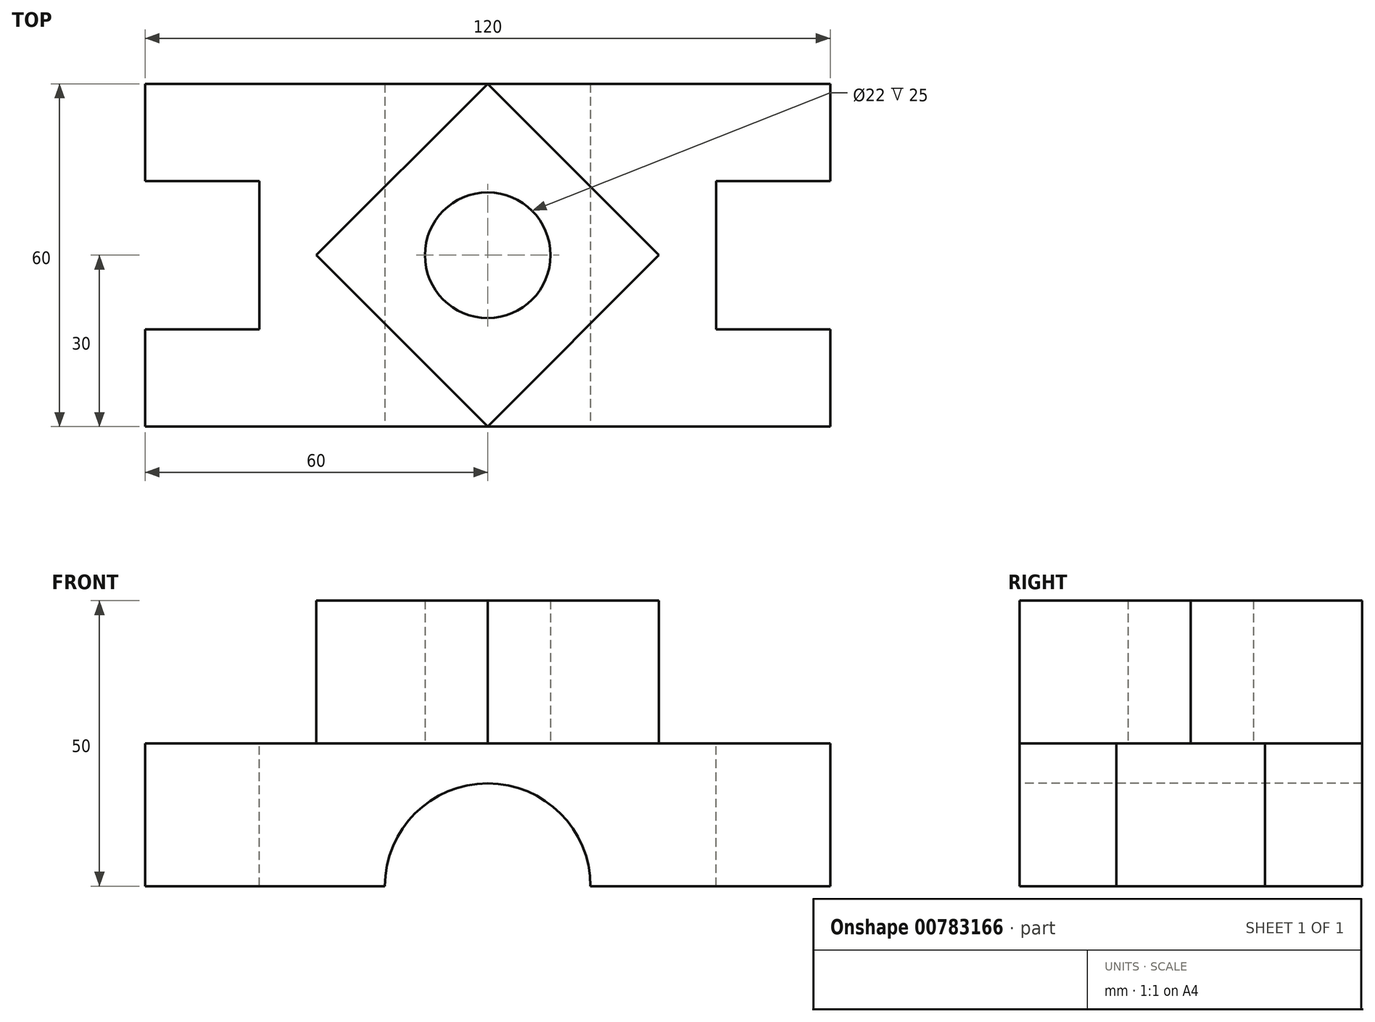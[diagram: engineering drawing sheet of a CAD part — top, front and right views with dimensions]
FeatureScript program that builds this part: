
annotation { "Feature Type Name" : "Feature", "Feature Type Description" : "" }
export const myFeature = defineFeature(function(context is Context, id is Id, definition is map)
    precondition{}
    {
        {
            var Q0;
            Q0=qCreatedBy(makeId("Top.planeOp"),FACE);
            var sketch = newSketch(context, id + "F0", { "sketchPlane" : qUnion([Q0])});
            skLineSegment(sketch, "E0.bottom", {"start": v(60, -30) * mm, "end": v(-60, -30) * mm});
            skLineSegment(sketch, "E0.top", {"start": v(60, 30) * mm, "end": v(-60, 30) * mm});
            skLineSegment(sketch, "E0.left", {"start": v(60, -30) * mm, "end": v(60, 30) * mm});
            skLineSegment(sketch, "E0.right", {"start": v(-60, -30) * mm, "end": v(-60, 30) * mm});
            skPoint(sketch, "E0.middle", {"position": v(0, 0) * mm});
            skSolve(sketch);
        }
        {
            var Q0;
            Q0=makeQuery(id+"F0.imprint","IMPRINT",FACE,{"disambiguationData":[TD([[makeQuery(id+"F0.imprint","IMPRINT",EDGE,{"derivedFrom":sQuery(id+"F0.wireOp",EDGE,"E0.bottom")}),-1.0]])]});
            extrude(context, id + "F1", {"entities" : qUnion([Q0]), "depth" : 25 * mm, "offsetDistance" : 25 * mm});
        }
        {
            var Q0;
            Q0=makeQuery(id+"F1.opExtrude","CAP_FACE",FACE,{"disambiguationData":[OSD([sQuery(id+"F0.wireOp",EDGE,"E0.bottom"),sQuery(id+"F0.wireOp",EDGE,"E0.top"),sQuery(id+"F0.wireOp",EDGE,"E0.left"),sQuery(id+"F0.wireOp",EDGE,"E0.right")])],"isStart":false});
            var sketch = newSketch(context, id + "F2", { "sketchPlane" : qUnion([Q0])});
            skLineSegment(sketch, "E1.bottom", {"start": v(80, -13) * mm, "end": v(40, -13) * mm});
            skLineSegment(sketch, "E1.top", {"start": v(80, 13) * mm, "end": v(40, 13) * mm});
            skLineSegment(sketch, "E1.left", {"start": v(80, -13) * mm, "end": v(80, 13) * mm});
            skLineSegment(sketch, "E1.right", {"start": v(40, -13) * mm, "end": v(40, 13) * mm});
            skPoint(sketch, "E1.middle", {"position": v(60, 0) * mm});
            skSolve(sketch);
        }
        {
            var Q0;
            {var subQ0=sQuery(id+"F2.wireOp",EDGE,"E1.right");Q0=makeQuery(id+"F2.imprint","IMPRINT",FACE,{"disambiguationData":[TD([[makeQuery(id+"F2.imprint","IMPRINT",EDGE,{"derivedFrom":subQ0}),-1.0]])]});}
            extrude(context, id + "F3", {"entities" : qUnion([Q0]), "operationType" : NewBodyOperationType.REMOVE, "endBound" : BoundingType.THROUGH_ALL, "oppositeDirection" : true, "depth" : 25 * mm, "offsetDistance" : 25 * mm});
        }
        {
            var Q0;
            Q0=makeQuery(id+"F1.opExtrude","CAP_FACE",FACE,{"disambiguationData":[OSD([sQuery(id+"F0.wireOp",EDGE,"E0.bottom"),sQuery(id+"F0.wireOp",EDGE,"E0.top"),sQuery(id+"F0.wireOp",EDGE,"E0.left"),sQuery(id+"F0.wireOp",EDGE,"E0.right")])],"isStart":false});
            var sketch = newSketch(context, id + "F4", { "sketchPlane" : qUnion([Q0])});
            skLineSegment(sketch, "E2.bottom", {"start": v(-40, -13) * mm, "end": v(-80, -13) * mm});
            skLineSegment(sketch, "E2.top", {"start": v(-40, 13) * mm, "end": v(-80, 13) * mm});
            skLineSegment(sketch, "E2.left", {"start": v(-40, -13) * mm, "end": v(-40, 13) * mm});
            skLineSegment(sketch, "E2.right", {"start": v(-80, -13) * mm, "end": v(-80, 13) * mm});
            skPoint(sketch, "E2.middle", {"position": v(-60, 0) * mm});
            skSolve(sketch);
        }
        {
            var Q0;
            {var subQ0=sQuery(id+"F4.wireOp",EDGE,"E2.left");Q0=makeQuery(id+"F4.imprint","IMPRINT",FACE,{"disambiguationData":[TD([[makeQuery(id+"F4.imprint","IMPRINT",EDGE,{"derivedFrom":subQ0}),1.0]])]});}
            extrude(context, id + "F5", {"entities" : qUnion([Q0]), "operationType" : NewBodyOperationType.REMOVE, "endBound" : BoundingType.THROUGH_ALL, "oppositeDirection" : true, "depth" : 25 * mm, "offsetDistance" : 25 * mm});
        }
        {
            var Q0;
            Q0=makeQuery(id+"F1.opExtrude","SWEPT_FACE",FACE,{"disambiguationData":[OSD([sQuery(id+"F0.wireOp",EDGE,"E0.bottom")])]});
            var sketch = newSketch(context, id + "F6", { "sketchPlane" : qUnion([Q0])});
            skCircle(sketch, "E3", {"center": v(0, 0) * mm, "radius": 18 * mm});
            skSolve(sketch);
        }
        {
            var Q0;
            {var subQ0=sQuery(id+"F6.wireOp",EDGE,"E3");var subQ1=makeQuery(id+"F1.opExtrude","CAP_EDGE",EDGE,{"disambiguationData":[OSD([sQuery(id+"F0.wireOp",EDGE,"E0.bottom")])],"isStart":true});var subQ2=makeQuery(id+"F6.imprint","INTERSECT",VERTEX,{"disambiguationData":[OD(0.0)],"derivedFrom":[subQ1,subQ0]});Q0=makeQuery(id+"F6.imprint","IMPRINT",FACE,{"disambiguationData":[TD([[makeQuery(id+"F6.imprint","IMPRINT",EDGE,{"disambiguationData":[TD([[subQ2,-1.0]])],"derivedFrom":subQ0}),1.0]])]});}
            extrude(context, id + "F7", {"entities" : qUnion([Q0]), "operationType" : NewBodyOperationType.REMOVE, "oppositeDirection" : true, "depth" : 25 * mm, "offsetDistance" : 25 * mm});
        }
        {
            var Q0;
            Q0=makeQuery(id+"F7.boolean.opBoolean","COPY",FACE,{"derivedFrom":makeQuery(id+"F7.opExtrude","CAP_FACE",FACE,{"disambiguationData":[OSD([sQuery(id+"F0.wireOp",EDGE,"E0.bottom"),sQuery(id+"F6.wireOp",EDGE,"E3")])],"isStart":false})});
            extrude(context, id + "F8", {"entities" : qUnion([Q0]), "operationType" : NewBodyOperationType.REMOVE, "endBound" : BoundingType.THROUGH_ALL, "oppositeDirection" : true, "depth" : 25 * mm, "offsetDistance" : 25 * mm});
        }
        {
            var Q0;
            Q0=makeQuery(id+"F1.opExtrude","CAP_FACE",FACE,{"disambiguationData":[OSD([sQuery(id+"F0.wireOp",EDGE,"E0.bottom"),sQuery(id+"F0.wireOp",EDGE,"E0.top"),sQuery(id+"F0.wireOp",EDGE,"E0.left"),sQuery(id+"F0.wireOp",EDGE,"E0.right")])],"isStart":false});
            var sketch = newSketch(context, id + "F9", { "sketchPlane" : qUnion([Q0])});
            skCircle(sketch, "E4", {"center": v(0, 0) * mm, "radius": 11 * mm});
            skLineSegment(sketch, "E5", {"start": v(0, 30) * mm, "end": v(0, -30) * mm});
            skLineSegment(sketch, "E6", {"start": v(0, -30) * mm, "end": v(-30, 0) * mm});
            skLineSegment(sketch, "E7", {"start": v(-30, 0) * mm, "end": v(30, 0) * mm});
            skLineSegment(sketch, "E8", {"start": v(30, 0) * mm, "end": v(0, -30) * mm});
            skLineSegment(sketch, "E9", {"start": v(0, 30) * mm, "end": v(30, 0) * mm});
            skLineSegment(sketch, "E10", {"start": v(0, 30) * mm, "end": v(-30, 0) * mm});
            skSolve(sketch);
        }
        {
            var Q0;
            {var subQ5=sQuery(id+"F9.wireOp",EDGE,"E9");Q0=makeQuery(id+"F9.imprint","IMPRINT",FACE,{"disambiguationData":[TD([[makeQuery(id+"F9.imprint","IMPRINT",EDGE,{"derivedFrom":subQ5}),-1.0]])]});}
            var Q1;
            {var subQ5=sQuery(id+"F9.wireOp",EDGE,"E10");Q1=makeQuery(id+"F9.imprint","IMPRINT",FACE,{"disambiguationData":[TD([[makeQuery(id+"F9.imprint","IMPRINT",EDGE,{"derivedFrom":subQ5}),1.0]])]});}
            var Q2;
            {var subQ5=sQuery(id+"F9.wireOp",EDGE,"E6");Q2=makeQuery(id+"F9.imprint","IMPRINT",FACE,{"disambiguationData":[TD([[makeQuery(id+"F9.imprint","IMPRINT",EDGE,{"derivedFrom":subQ5}),-1.0]])]});}
            var Q3;
            {var subQ5=sQuery(id+"F9.wireOp",EDGE,"E8");Q3=makeQuery(id+"F9.imprint","IMPRINT",FACE,{"disambiguationData":[TD([[makeQuery(id+"F9.imprint","IMPRINT",EDGE,{"derivedFrom":subQ5}),-1.0]])]});}
            extrude(context, id + "F10", {"entities" : qUnion([Q0, Q1, Q2, Q3]), "operationType" : NewBodyOperationType.ADD, "depth" : 25 * mm, "offsetDistance" : 25 * mm});
        }
    });
